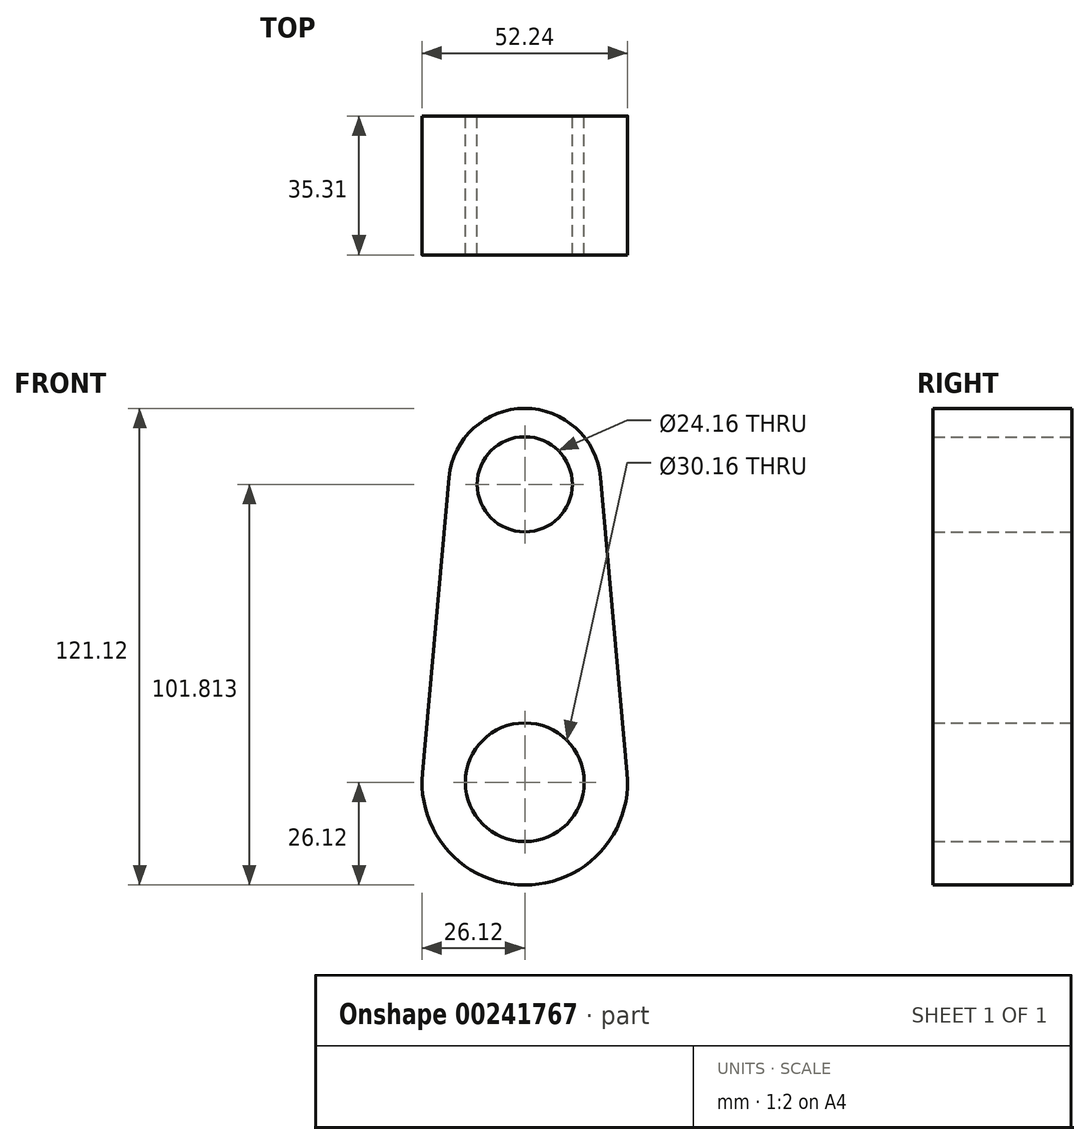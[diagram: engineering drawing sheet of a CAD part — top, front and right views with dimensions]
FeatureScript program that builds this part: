
annotation { "Feature Type Name" : "Feature", "Feature Type Description" : "" }
export const myFeature = defineFeature(function(context is Context, id is Id, definition is map)
    precondition{}
    {
        {
            var Q0;
            Q0=qCreatedBy(makeId("Front.planeOp"),FACE);
            var sketch = newSketch(context, id + "F0", { "sketchPlane" : qUnion([Q0])});
            skCircle(sketch, "E0", {"center": v(0, 45.47) * mm, "radius": 12.08 * mm});
            skCircle(sketch, "E1", {"center": v(0, -30.22) * mm, "radius": 15.08 * mm});
            skArc(sketch, "E2", {"start": v(19.23, 47.21) * mm, "mid": v(0, 64.78) * mm, "end": v(-19.23, 47.21) * mm});
            skArc(sketch, "E3", {"start": v(-26.01, -27.87) * mm, "mid": v(0, -56.34) * mm, "end": v(26.01, -27.87) * mm});
            skLineSegment(sketch, "E4", {"start": v(-19.23, 47.21) * mm, "end": v(-26.01, -27.87) * mm});
            skLineSegment(sketch, "E5", {"start": v(19.23, 47.21) * mm, "end": v(26.01, -27.87) * mm});
            skSolve(sketch);
        }
        {
            var Q0;
            Q0=makeQuery(id+"F0.imprint","IMPRINT",FACE,{"disambiguationData":[TD([[makeQuery(id+"F0.imprint","IMPRINT",EDGE,{"derivedFrom":sQuery(id+"F0.wireOp",EDGE,"E0")}),-1.0]])]});
            extrude(context, id + "F1", {"entities" : qUnion([Q0]), "depth" : 35.3 * mm});
        }
    });
